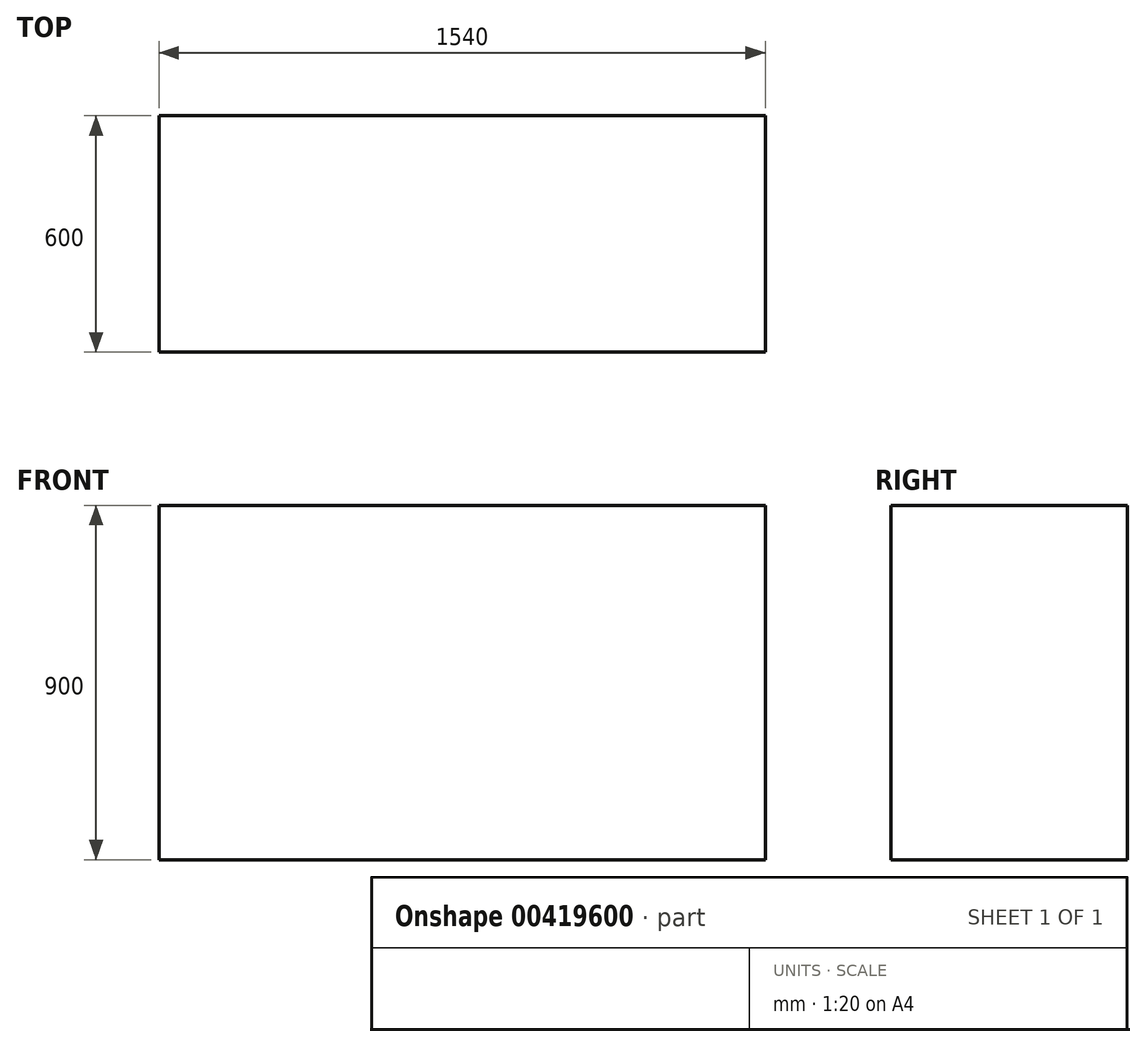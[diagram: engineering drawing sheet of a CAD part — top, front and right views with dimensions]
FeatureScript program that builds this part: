
annotation { "Feature Type Name" : "Feature", "Feature Type Description" : "" }
export const myFeature = defineFeature(function(context is Context, id is Id, definition is map)
    precondition{}
    {
        {
            var Q0;
            Q0=qCreatedBy(makeId("Top.planeOp"),FACE);
            var sketch = newSketch(context, id + "F0", { "sketchPlane" : qUnion([Q0])});
            skLineSegment(sketch, "E0.bottom", {"start": v(-1442.4, 543.55) * mm, "end": v(97.6, 543.55) * mm});
            skLineSegment(sketch, "E0.top", {"start": v(-1442.4, -56.45) * mm, "end": v(97.6, -56.45) * mm});
            skLineSegment(sketch, "E0.left", {"start": v(-1442.4, 543.55) * mm, "end": v(-1442.4, -56.45) * mm});
            skLineSegment(sketch, "E0.right", {"start": v(97.6, 543.55) * mm, "end": v(97.6, -56.45) * mm});
            skSolve(sketch);
        }
        {
            var Q0;
            Q0=makeQuery(id+"F0.imprint","IMPRINT",FACE,{"disambiguationData":[TD([[makeQuery(id+"F0.imprint","IMPRINT",EDGE,{"derivedFrom":sQuery(id+"F0.wireOp",EDGE,"E0.bottom")}),-1.0]])]});
            extrude(context, id + "F1", {"entities" : qUnion([Q0]), "depth" : 900 * mm});
        }
    });
